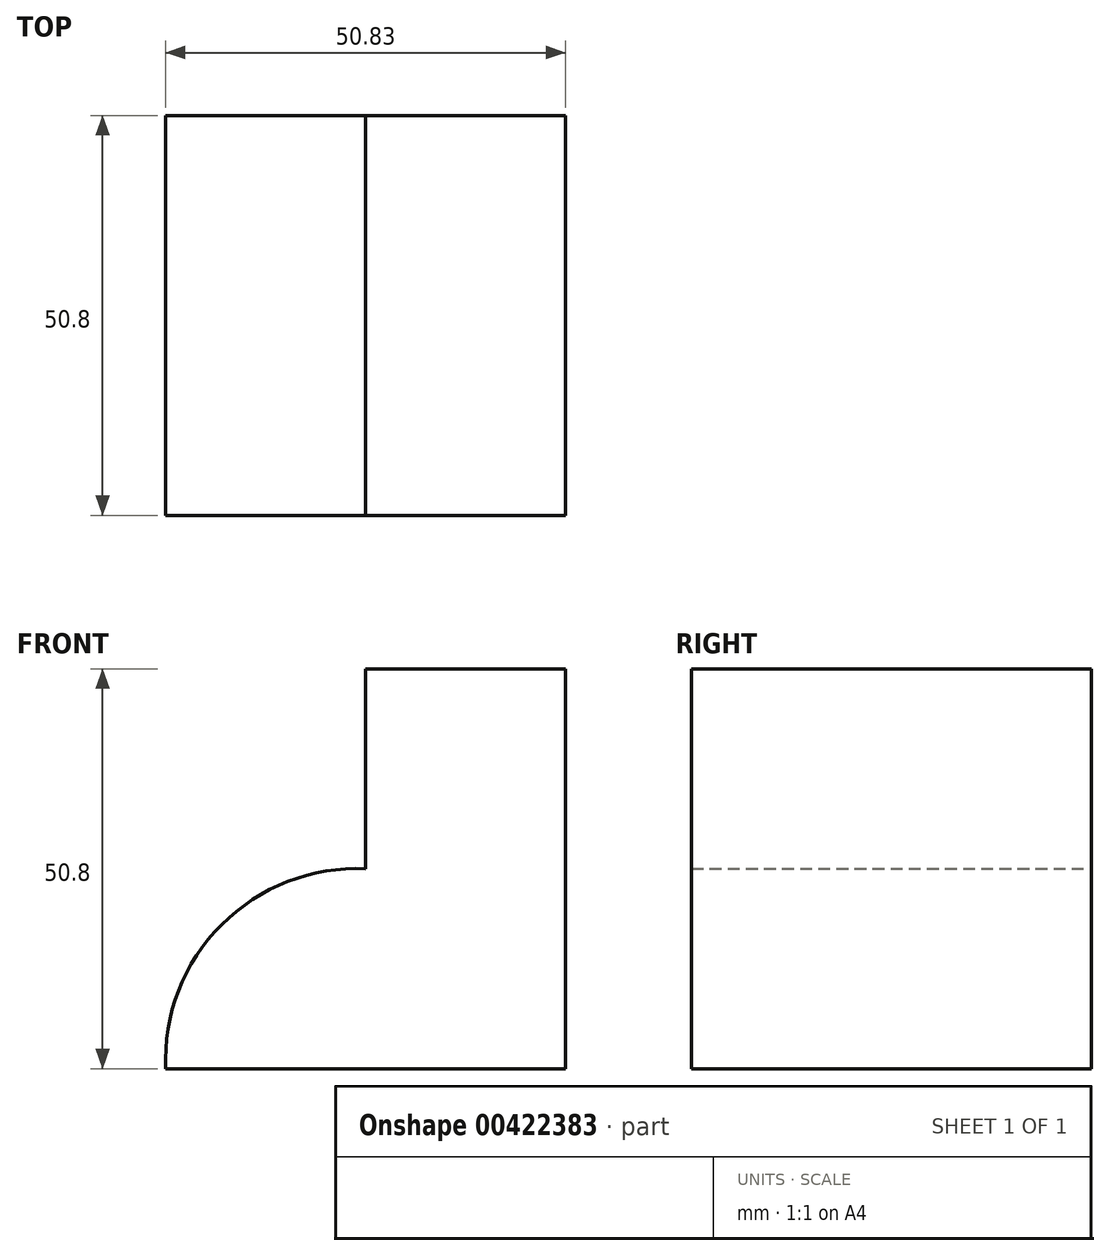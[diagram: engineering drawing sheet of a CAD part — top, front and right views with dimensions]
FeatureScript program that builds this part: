
annotation { "Feature Type Name" : "Feature", "Feature Type Description" : "" }
export const myFeature = defineFeature(function(context is Context, id is Id, definition is map)
    precondition{}
    {
        {
            var Q0;
            Q0=qCreatedBy(makeId("Front.planeOp"),FACE);
            var sketch = newSketch(context, id + "F0", { "sketchPlane" : qUnion([Q0])});
            skLineSegment(sketch, "E0", {"start": v(-27.61, 2.85) * mm, "end": v(-27.61, 28.25) * mm});
            skLineSegment(sketch, "E1", {"start": v(-27.61, 28.25) * mm, "end": v(-2.21, 28.25) * mm});
            skLineSegment(sketch, "E2", {"start": v(-2.21, 28.25) * mm, "end": v(-2.21, -22.55) * mm});
            skLineSegment(sketch, "E3", {"start": v(-2.21, -22.55) * mm, "end": v(-53.01, -22.55) * mm});
            skArc(sketch, "E4", {"start": v(-27.61, 2.85) * mm, "mid": v(-45.91, -4.26) * mm, "end": v(-53.01, -22.55) * mm});
            skSolve(sketch);
        }
        {
            var Q0;
            Q0=makeQuery(id+"F0.imprint","IMPRINT",FACE,{"disambiguationData":[TD([[makeQuery(id+"F0.imprint","IMPRINT",EDGE,{"derivedFrom":sQuery(id+"F0.wireOp",EDGE,"E0")}),-1.0]])]});
            extrude(context, id + "F1", {"entities" : qUnion([Q0]), "depth" : 50.8 * mm});
        }
    });
